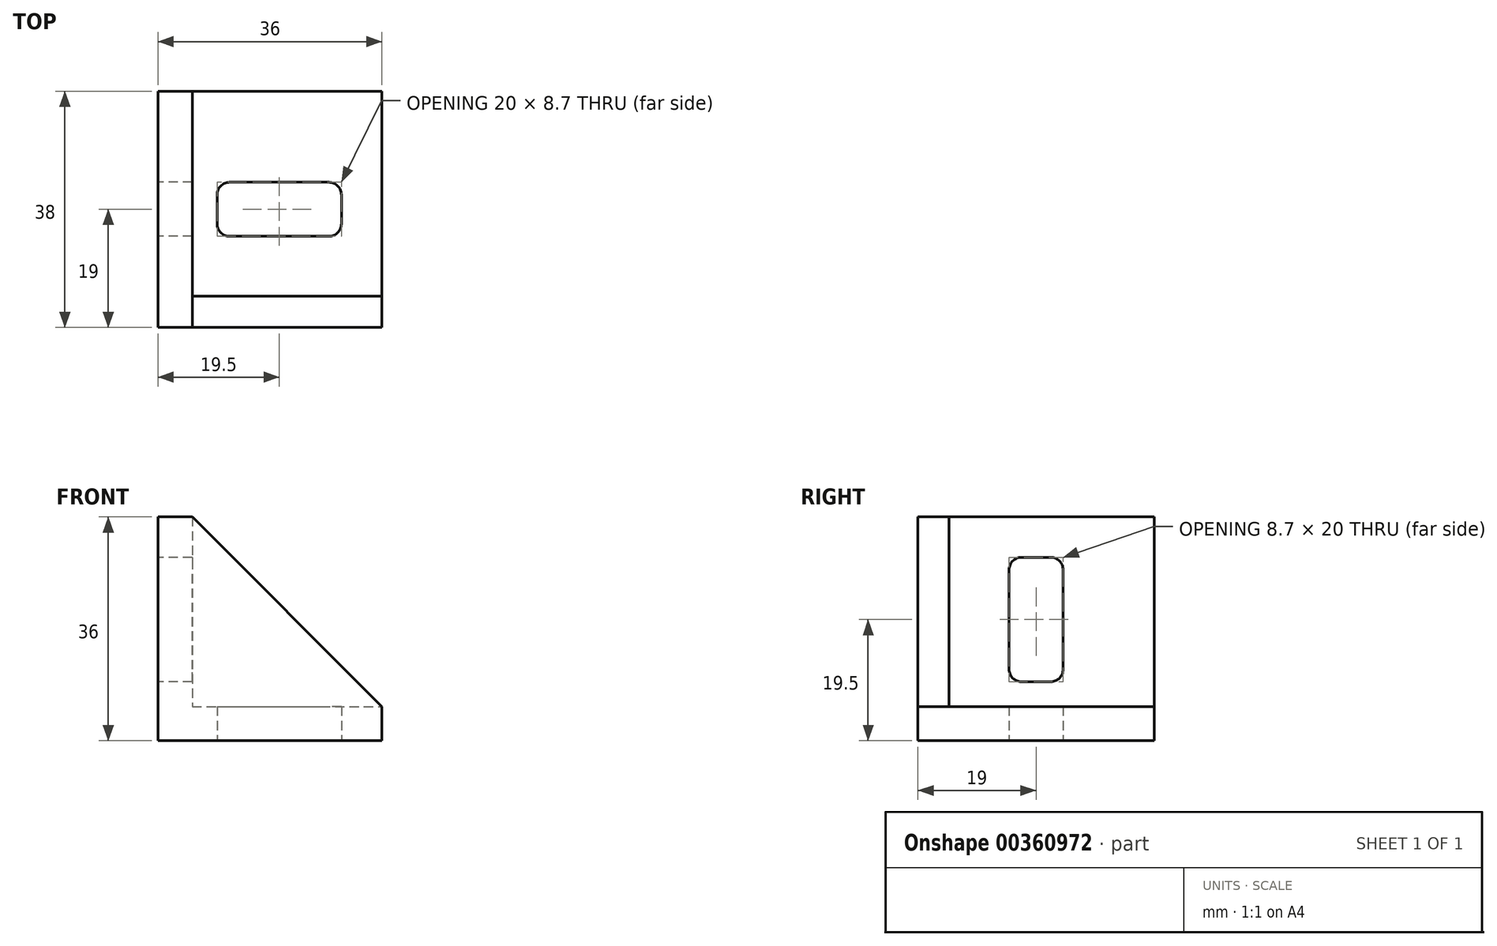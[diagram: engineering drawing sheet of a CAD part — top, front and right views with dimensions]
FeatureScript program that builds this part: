
annotation { "Feature Type Name" : "Feature", "Feature Type Description" : "" }
export const myFeature = defineFeature(function(context is Context, id is Id, definition is map)
    precondition{}
    {
        {
            var Q0;
            Q0=qCreatedBy(makeId("Top.planeOp"),FACE);
            var sketch = newSketch(context, id + "F0", { "sketchPlane" : qUnion([Q0])});
            skLineSegment(sketch, "E0.bottom", {"start": v(18, 19) * mm, "end": v(-18, 19) * mm});
            skLineSegment(sketch, "E0.top", {"start": v(18, -19) * mm, "end": v(-18, -19) * mm});
            skLineSegment(sketch, "E0.left", {"start": v(18, 19) * mm, "end": v(18, -19) * mm});
            skLineSegment(sketch, "E0.right", {"start": v(-18, 19) * mm, "end": v(-18, -19) * mm});
            skPoint(sketch, "E0.middle", {"position": v(0, 0) * mm});
            skLineSegment(sketch, "E1", {"start": v(-18, 0) * mm, "end": v(18, 0) * mm, "construction": true});
            skLineSegment(sketch, "E2.bottom", {"start": v(-6.5, 4.35) * mm, "end": v(9.5, 4.35) * mm});
            skLineSegment(sketch, "E2.top", {"start": v(-6.5, -4.35) * mm, "end": v(9.5, -4.35) * mm});
            skLineSegment(sketch, "E2.left", {"start": v(-8.5, 2.35) * mm, "end": v(-8.5, -2.35) * mm});
            skLineSegment(sketch, "E2.right", {"start": v(11.5, 2.35) * mm, "end": v(11.5, -2.35) * mm});
            skPoint(sketch, "E3.visualSharp", {"position": v(-8.5, 4.35) * mm});
            skArc(sketch, "E3.filletArc", {"start": v(-6.5, 4.35) * mm, "mid": v(-7.91, 3.76) * mm, "end": v(-8.5, 2.35) * mm});
            skPoint(sketch, "E4.visualSharp", {"position": v(-8.5, -4.35) * mm});
            skArc(sketch, "E4.filletArc", {"start": v(-8.5, -2.35) * mm, "mid": v(-7.91, -3.76) * mm, "end": v(-6.5, -4.35) * mm});
            skPoint(sketch, "E5.visualSharp", {"position": v(11.5, -4.35) * mm});
            skArc(sketch, "E5.filletArc", {"start": v(9.5, -4.35) * mm, "mid": v(10.91, -3.76) * mm, "end": v(11.5, -2.35) * mm});
            skPoint(sketch, "E6.visualSharp", {"position": v(11.5, 4.35) * mm});
            skArc(sketch, "E6.filletArc", {"start": v(11.5, 2.35) * mm, "mid": v(10.91, 3.76) * mm, "end": v(9.5, 4.35) * mm});
            skPoint(sketch, "E7", {"position": v(-18, 11.4) * mm});
            skPoint(sketch, "E8", {"position": v(-18, -11.4) * mm});
            skSolve(sketch);
        }
        {
            var Q0;
            Q0=makeQuery(id+"F0.imprint","IMPRINT",FACE,{"disambiguationData":[TD([[makeQuery(id+"F0.imprint","IMPRINT",EDGE,{"derivedFrom":sQuery(id+"F0.wireOp",EDGE,"E0.bottom")}),1.0]])]});
            extrude(context, id + "F1", {"entities" : qUnion([Q0]), "depth" : 36 * mm});
        }
        {
            var Q0;
            Q0=makeQuery(id+"F1.opExtrude","SWEPT_FACE",FACE,{"disambiguationData":[OSD([sQuery(id+"F0.wireOp",EDGE,"E0.bottom")])]});
            var sketch = newSketch(context, id + "F2", { "sketchPlane" : qUnion([Q0])});
            skLineSegment(sketch, "E9", {"start": v(18, 36) * mm, "end": v(12.5, 36) * mm});
            skLineSegment(sketch, "E10", {"start": v(12.5, 36) * mm, "end": v(12.5, 5.5) * mm});
            skLineSegment(sketch, "E11", {"start": v(12.5, 5.5) * mm, "end": v(-18, 5.5) * mm});
            skLineSegment(sketch, "E12", {"start": v(-18, 5.5) * mm, "end": v(-18, 0) * mm});
            skLineSegment(sketch, "E13", {"start": v(-18, 0) * mm, "end": v(18, 0) * mm});
            skLineSegment(sketch, "E14", {"start": v(18, 0) * mm, "end": v(18, 36) * mm});
            skLineSegment(sketch, "E15", {"start": v(12.5, 36) * mm, "end": v(-18, 5.5) * mm});
            skSolve(sketch);
        }
        {
            var Q0;
            {var subQ0=sQuery(id+"F2.wireOp",EDGE,"E15");Q0=makeQuery(id+"F2.imprint","IMPRINT",FACE,{"disambiguationData":[TD([[makeQuery(id+"F2.imprint","IMPRINT",EDGE,{"derivedFrom":subQ0}),-1.0]])]});}
            extrude(context, id + "F3", {"entities" : qUnion([Q0]), "operationType" : NewBodyOperationType.REMOVE, "endBound" : BoundingType.THROUGH_ALL, "oppositeDirection" : true, "depth" : 25 * mm});
        }
        {
            var Q0;
            Q0=makeQuery(id+"F2.imprint","IMPRINT",FACE,{"disambiguationData":[TD([[makeQuery(id+"F2.imprint","IMPRINT",EDGE,{"derivedFrom":sQuery(id+"F2.wireOp",EDGE,"E10")}),-1.0]])]});
            extrude(context, id + "F4", {"entities" : qUnion([Q0]), "operationType" : NewBodyOperationType.REMOVE, "oppositeDirection" : true, "depth" : 33 * mm});
        }
        {
            var Q0;
            Q0=makeQuery(id+"F1.opExtrude","SWEPT_FACE",FACE,{"disambiguationData":[OSD([sQuery(id+"F0.wireOp",EDGE,"E0.right")])]});
            var sketch = newSketch(context, id + "F5", { "sketchPlane" : qUnion([Q0])});
            skLineSegment(sketch, "E16.bottom", {"start": v(-2.35, 29.5) * mm, "end": v(2.35, 29.5) * mm});
            skLineSegment(sketch, "E16.top", {"start": v(-2.35, 9.5) * mm, "end": v(2.35, 9.5) * mm});
            skLineSegment(sketch, "E16.left", {"start": v(-4.35, 27.5) * mm, "end": v(-4.35, 11.5) * mm});
            skLineSegment(sketch, "E16.right", {"start": v(4.35, 27.5) * mm, "end": v(4.35, 11.5) * mm});
            skLineSegment(sketch, "E17", {"start": v(0, 0) * mm, "end": v(0, 36) * mm, "construction": true});
            skPoint(sketch, "E18.visualSharp", {"position": v(-4.35, 9.5) * mm});
            skArc(sketch, "E18.filletArc", {"start": v(-4.35, 11.5) * mm, "mid": v(-3.76, 10.09) * mm, "end": v(-2.35, 9.5) * mm});
            skPoint(sketch, "E19.visualSharp", {"position": v(-4.35, 29.5) * mm});
            skArc(sketch, "E19.filletArc", {"start": v(-2.35, 29.5) * mm, "mid": v(-3.76, 28.91) * mm, "end": v(-4.35, 27.5) * mm});
            skPoint(sketch, "E20.visualSharp", {"position": v(4.35, 29.5) * mm});
            skArc(sketch, "E20.filletArc", {"start": v(4.35, 27.5) * mm, "mid": v(3.76, 28.91) * mm, "end": v(2.35, 29.5) * mm});
            skPoint(sketch, "E21.visualSharp", {"position": v(4.35, 9.5) * mm});
            skArc(sketch, "E21.filletArc", {"start": v(2.35, 9.5) * mm, "mid": v(3.76, 10.09) * mm, "end": v(4.35, 11.5) * mm});
            skSolve(sketch);
        }
        {
            var Q0;
            Q0=makeQuery(id+"F5.imprint","IMPRINT",FACE,{"disambiguationData":[TD([[makeQuery(id+"F5.imprint","IMPRINT",EDGE,{"derivedFrom":sQuery(id+"F5.wireOp",EDGE,"E16.bottom")}),-1.0]])]});
            extrude(context, id + "F6", {"entities" : qUnion([Q0]), "operationType" : NewBodyOperationType.REMOVE, "endBound" : BoundingType.THROUGH_ALL, "oppositeDirection" : true, "depth" : 25 * mm});
        }
    });
